# Revit family: Lotus S Barstool
name_source: partatom
category: Furniture
revit_build: Autodesk Revit 2017 (Build: 20160225_1515(x64)
units: mm (PartAtom-declared; Revit-internal decimal feet)

## family parameters
Always vertical = Yes
Cut with Voids When Loaded = No
OmniClass Number = 23.40.20.00
OmniClass Title = General Furniture and Specialties
Room Calculation Point = No
Shared = No
Work Plane-Based = No

## types (1)
- Lotus S Barstool
    Assembly Code = E2020200
    Assistance = Call for assistance number: 336.941.3446
    Barstool type = Bar height, 4-Leg
    Collection = Lotus
    Depth = 21 mm
    Description = Barstool with metal frame, upholstered seat and wood back panel and spindles
    Height = 42 mm
    Industry = Restaurant, Hotel, College
    Length = 19 mm  [stored 0.062336 ft]
    Manufacturer = Beaufurn
    Manufacturer Country = USA
    Model = Lotus S Barstool
    Products of collection = Lotus Chairs, Lotus Barstools
    Seat depth = 16 mm
    Seat height = 31 mm
    Secondary structure material = Standard wood finishes or Cof
    Structure material = Selected powdercoat color or any RAL color
    Type Comments = Suitable for Restaurants, Hotels and Universities
    URL = http://beaufurn.com
    Upholstery material = Graded Fabric or Com
    Usage = Indoor
    Yardage = 1 mm  [stored 0.00328084 ft]

note: [stored X ft] marks values corroborated as IEEE doubles in the binary element streams (Revit-internal decimal feet)

## geometry (parser evidence)
native form markers: Sweep x2
no freeform markers — native parametric forms only
